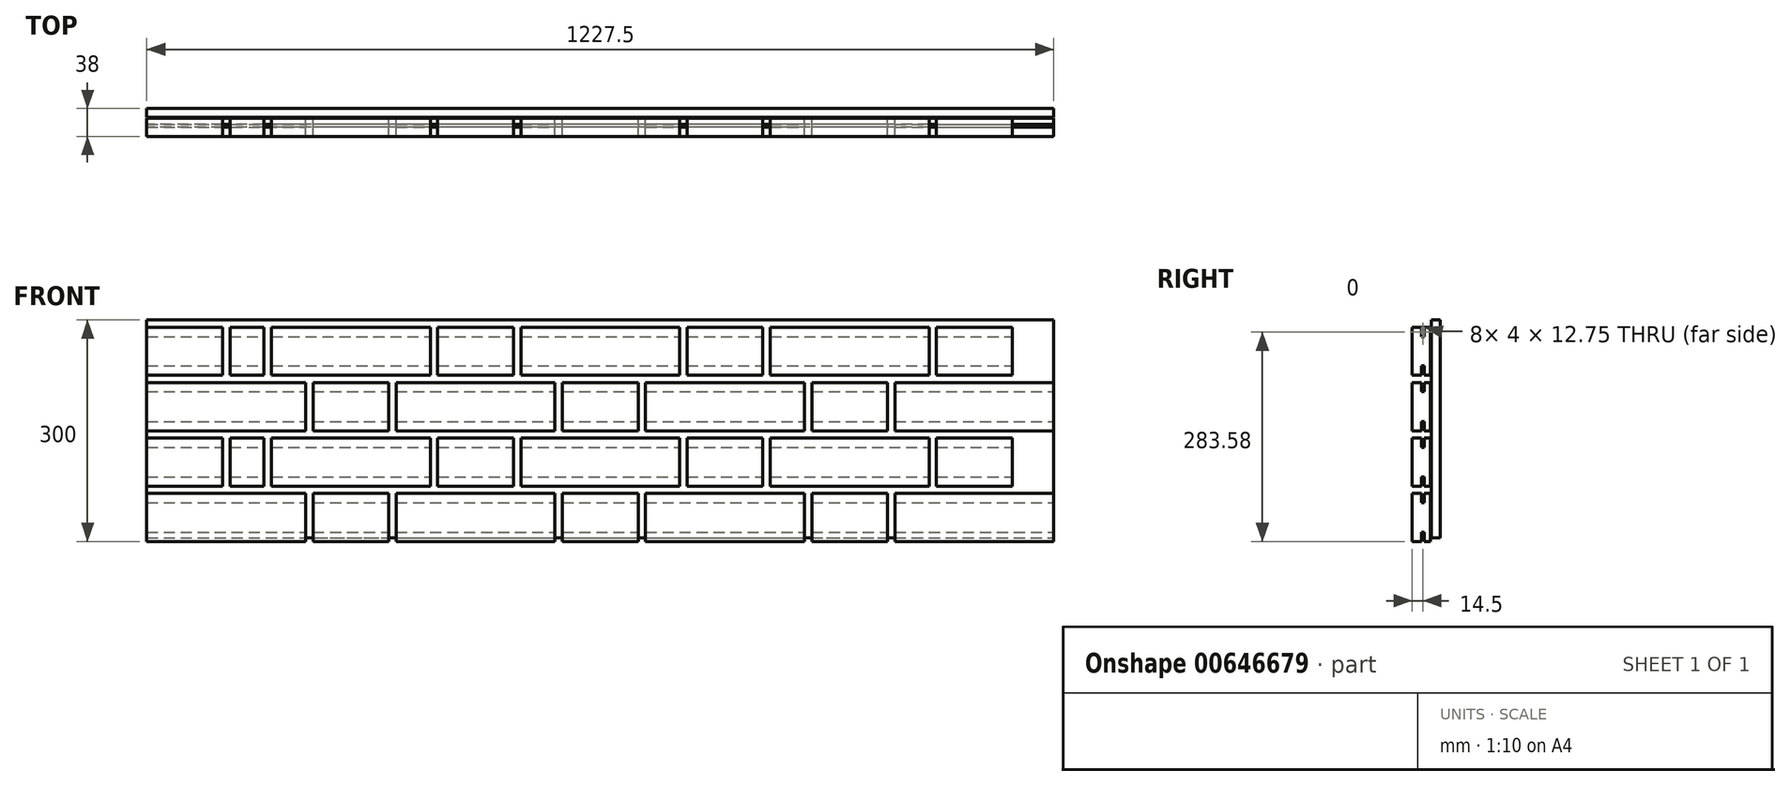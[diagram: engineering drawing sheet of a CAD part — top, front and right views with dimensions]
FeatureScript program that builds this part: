
annotation { "Feature Type Name" : "Feature", "Feature Type Description" : "" }
export const myFeature = defineFeature(function(context is Context, id is Id, definition is map)
    precondition{}
    {
        {
            var Q0;
            Q0=qCreatedBy(makeId("Front.planeOp"),FACE);
            var sketch = newSketch(context, id + "F0", { "sketchPlane" : qUnion([Q0])});
            skLineSegment(sketch, "E0", {"start": v(-1075.67, 0) * mm, "end": v(-1075.67, 65) * mm});
            skLineSegment(sketch, "E1", {"start": v(-1628.17, 150) * mm, "end": v(-1413.17, 150) * mm});
            skLineSegment(sketch, "E2", {"start": v(-1413.17, 150) * mm, "end": v(-1413.17, 215) * mm});
            skLineSegment(sketch, "E3", {"start": v(-1413.17, 215) * mm, "end": v(-1628.17, 215) * mm});
            skLineSegment(sketch, "E4", {"start": v(-1628.17, 215) * mm, "end": v(-1628.17, 150) * mm});
            skLineSegment(sketch, "E5", {"start": v(-1403.17, 150) * mm, "end": v(-1300.67, 150) * mm});
            skLineSegment(sketch, "E6", {"start": v(-1300.67, 150) * mm, "end": v(-1300.67, 215) * mm});
            skLineSegment(sketch, "E7", {"start": v(-1300.67, 215) * mm, "end": v(-1403.17, 215) * mm});
            skLineSegment(sketch, "E8", {"start": v(-1403.17, 215) * mm, "end": v(-1403.17, 150) * mm});
            skLineSegment(sketch, "E9", {"start": v(-1290.67, 150) * mm, "end": v(-1075.67, 150) * mm});
            skLineSegment(sketch, "E10", {"start": v(-1075.67, 150) * mm, "end": v(-1075.67, 215) * mm});
            skLineSegment(sketch, "E11", {"start": v(-1075.67, 215) * mm, "end": v(-1290.67, 215) * mm});
            skLineSegment(sketch, "E12", {"start": v(-1290.67, 215) * mm, "end": v(-1290.67, 150) * mm});
            skLineSegment(sketch, "E13", {"start": v(-2078.17, 150) * mm, "end": v(-1975.67, 150) * mm});
            skLineSegment(sketch, "E14", {"start": v(-1975.67, 150) * mm, "end": v(-1975.67, 215) * mm});
            skLineSegment(sketch, "E15", {"start": v(-1975.67, 215) * mm, "end": v(-2078.17, 215) * mm});
            skLineSegment(sketch, "E16", {"start": v(-2078.17, 215) * mm, "end": v(-2078.17, 150) * mm});
            skLineSegment(sketch, "E17", {"start": v(-1965.67, 150) * mm, "end": v(-1750.67, 150) * mm});
            skLineSegment(sketch, "E18", {"start": v(-1750.67, 150) * mm, "end": v(-1750.67, 215) * mm});
            skLineSegment(sketch, "E19", {"start": v(-1750.67, 215) * mm, "end": v(-1965.67, 215) * mm});
            skLineSegment(sketch, "E20", {"start": v(-1965.67, 215) * mm, "end": v(-1965.67, 150) * mm});
            skLineSegment(sketch, "E21", {"start": v(-1740.67, 150) * mm, "end": v(-1638.17, 150) * mm});
            skLineSegment(sketch, "E22", {"start": v(-1638.17, 150) * mm, "end": v(-1638.17, 215) * mm});
            skLineSegment(sketch, "E23", {"start": v(-1638.17, 215) * mm, "end": v(-1740.67, 215) * mm});
            skLineSegment(sketch, "E24", {"start": v(-1740.67, 215) * mm, "end": v(-1740.67, 150) * mm});
            skLineSegment(sketch, "E25", {"start": v(-2088.17, 150) * mm, "end": v(-2303.17, 150) * mm});
            skLineSegment(sketch, "E26", {"start": v(-2303.17, 150) * mm, "end": v(-2303.17, 215) * mm});
            skLineSegment(sketch, "E27", {"start": v(-2303.17, 215) * mm, "end": v(-2088.17, 215) * mm});
            skLineSegment(sketch, "E28", {"start": v(-2088.17, 215) * mm, "end": v(-2088.17, 150) * mm});
            skLineSegment(sketch, "E29", {"start": v(-2303.17, 225) * mm, "end": v(-2200.67, 225) * mm});
            skLineSegment(sketch, "E30", {"start": v(-2200.67, 225) * mm, "end": v(-2200.67, 290) * mm});
            skLineSegment(sketch, "E31", {"start": v(-2200.67, 290) * mm, "end": v(-2303.17, 290) * mm});
            skLineSegment(sketch, "E32", {"start": v(-2303.17, 290) * mm, "end": v(-2303.17, 225) * mm});
            skLineSegment(sketch, "E33", {"start": v(-2134.42, 225) * mm, "end": v(-1919.42, 225) * mm});
            skLineSegment(sketch, "E34", {"start": v(-1919.42, 225) * mm, "end": v(-1919.42, 290) * mm});
            skLineSegment(sketch, "E35", {"start": v(-1919.42, 290) * mm, "end": v(-2134.42, 290) * mm});
            skLineSegment(sketch, "E36", {"start": v(-2134.42, 290) * mm, "end": v(-2134.42, 225) * mm});
            skLineSegment(sketch, "E37", {"start": v(-1909.42, 225) * mm, "end": v(-1806.92, 225) * mm});
            skLineSegment(sketch, "E38", {"start": v(-1806.92, 225) * mm, "end": v(-1806.92, 290) * mm});
            skLineSegment(sketch, "E39", {"start": v(-1806.92, 290) * mm, "end": v(-1909.42, 290) * mm});
            skLineSegment(sketch, "E40", {"start": v(-1909.42, 290) * mm, "end": v(-1909.42, 225) * mm});
            skLineSegment(sketch, "E41", {"start": v(-2190.67, 225) * mm, "end": v(-2144.37, 225) * mm});
            skLineSegment(sketch, "E42", {"start": v(-2144.37, 225) * mm, "end": v(-2144.37, 290) * mm});
            skLineSegment(sketch, "E43", {"start": v(-2144.37, 290) * mm, "end": v(-2190.67, 290) * mm});
            skLineSegment(sketch, "E44", {"start": v(-2190.67, 290) * mm, "end": v(-2190.67, 225) * mm});
            skLineSegment(sketch, "E45", {"start": v(-1796.92, 225) * mm, "end": v(-1581.92, 225) * mm});
            skLineSegment(sketch, "E46", {"start": v(-1581.92, 225) * mm, "end": v(-1581.92, 290) * mm});
            skLineSegment(sketch, "E47", {"start": v(-1581.92, 290) * mm, "end": v(-1796.92, 290) * mm});
            skLineSegment(sketch, "E48", {"start": v(-1796.92, 290) * mm, "end": v(-1796.92, 225) * mm});
            skLineSegment(sketch, "E49", {"start": v(-1571.92, 225) * mm, "end": v(-1469.42, 225) * mm});
            skLineSegment(sketch, "E50", {"start": v(-1469.42, 225) * mm, "end": v(-1469.42, 290) * mm});
            skLineSegment(sketch, "E51", {"start": v(-1469.42, 290) * mm, "end": v(-1571.92, 290) * mm});
            skLineSegment(sketch, "E52", {"start": v(-1571.92, 290) * mm, "end": v(-1571.92, 225) * mm});
            skLineSegment(sketch, "E53", {"start": v(-1459.42, 225) * mm, "end": v(-1244.42, 225) * mm});
            skLineSegment(sketch, "E54", {"start": v(-1244.42, 225) * mm, "end": v(-1244.42, 290) * mm});
            skLineSegment(sketch, "E55", {"start": v(-1244.42, 290) * mm, "end": v(-1459.42, 290) * mm});
            skLineSegment(sketch, "E56", {"start": v(-1459.42, 290) * mm, "end": v(-1459.42, 225) * mm});
            skLineSegment(sketch, "E57", {"start": v(-1234.42, 225) * mm, "end": v(-1131.92, 225) * mm});
            skLineSegment(sketch, "E58", {"start": v(-1131.92, 225) * mm, "end": v(-1131.92, 290) * mm});
            skLineSegment(sketch, "E59", {"start": v(-1131.92, 290) * mm, "end": v(-1234.42, 290) * mm});
            skLineSegment(sketch, "E60", {"start": v(-1234.42, 290) * mm, "end": v(-1234.42, 225) * mm});
            skLineSegment(sketch, "E61", {"start": v(-1628.17, 65) * mm, "end": v(-1413.17, 65) * mm});
            skLineSegment(sketch, "E62", {"start": v(-1413.17, 65) * mm, "end": v(-1413.17, 0) * mm});
            skLineSegment(sketch, "E63", {"start": v(-1413.17, 0) * mm, "end": v(-1628.17, 0) * mm});
            skLineSegment(sketch, "E64", {"start": v(-1628.17, 0) * mm, "end": v(-1628.17, 65) * mm});
            skLineSegment(sketch, "E65", {"start": v(-1403.17, 65) * mm, "end": v(-1300.67, 65) * mm});
            skLineSegment(sketch, "E66", {"start": v(-1300.67, 65) * mm, "end": v(-1300.67, 0) * mm});
            skLineSegment(sketch, "E67", {"start": v(-1300.67, 0) * mm, "end": v(-1403.17, 0) * mm});
            skLineSegment(sketch, "E68", {"start": v(-1403.17, 0) * mm, "end": v(-1403.17, 65) * mm});
            skLineSegment(sketch, "E69", {"start": v(-1290.67, 65) * mm, "end": v(-1075.67, 65) * mm});
            skLineSegment(sketch, "E70", {"start": v(-1075.67, 65) * mm, "end": v(-1075.67, 0) * mm});
            skLineSegment(sketch, "E71", {"start": v(-1075.67, 0) * mm, "end": v(-1290.67, 0) * mm});
            skLineSegment(sketch, "E72", {"start": v(-1290.67, 0) * mm, "end": v(-1290.67, 65) * mm});
            skLineSegment(sketch, "E73", {"start": v(-2078.17, 65) * mm, "end": v(-1975.67, 65) * mm});
            skLineSegment(sketch, "E74", {"start": v(-1975.67, 65) * mm, "end": v(-1975.67, 0) * mm});
            skLineSegment(sketch, "E75", {"start": v(-1975.67, 0) * mm, "end": v(-2078.17, 0) * mm});
            skLineSegment(sketch, "E76", {"start": v(-2078.17, 0) * mm, "end": v(-2078.17, 65) * mm});
            skLineSegment(sketch, "E77", {"start": v(-1965.67, 65) * mm, "end": v(-1750.67, 65) * mm});
            skLineSegment(sketch, "E78", {"start": v(-1750.67, 65) * mm, "end": v(-1750.67, 0) * mm});
            skLineSegment(sketch, "E79", {"start": v(-1750.67, 0) * mm, "end": v(-1965.67, 0) * mm});
            skLineSegment(sketch, "E80", {"start": v(-1965.67, 0) * mm, "end": v(-1965.67, 65) * mm});
            skLineSegment(sketch, "E81", {"start": v(-1740.67, 65) * mm, "end": v(-1638.17, 65) * mm});
            skLineSegment(sketch, "E82", {"start": v(-1638.17, 65) * mm, "end": v(-1638.17, 0) * mm});
            skLineSegment(sketch, "E83", {"start": v(-1638.17, 0) * mm, "end": v(-1740.67, 0) * mm});
            skLineSegment(sketch, "E84", {"start": v(-1740.67, 0) * mm, "end": v(-1740.67, 65) * mm});
            skLineSegment(sketch, "E85", {"start": v(-2088.17, 65) * mm, "end": v(-2303.17, 65) * mm});
            skLineSegment(sketch, "E86", {"start": v(-2303.17, 65) * mm, "end": v(-2303.17, 0) * mm});
            skLineSegment(sketch, "E87", {"start": v(-2303.17, 0) * mm, "end": v(-2088.17, 0) * mm});
            skLineSegment(sketch, "E88", {"start": v(-2088.17, 0) * mm, "end": v(-2088.17, 65) * mm});
            skLineSegment(sketch, "E89", {"start": v(-2303.17, 140) * mm, "end": v(-2200.67, 140) * mm});
            skLineSegment(sketch, "E90", {"start": v(-2200.67, 140) * mm, "end": v(-2200.67, 75) * mm});
            skLineSegment(sketch, "E91", {"start": v(-2200.67, 75) * mm, "end": v(-2303.17, 75) * mm});
            skLineSegment(sketch, "E92", {"start": v(-2303.17, 75) * mm, "end": v(-2303.17, 140) * mm});
            skLineSegment(sketch, "E93", {"start": v(-2134.42, 140) * mm, "end": v(-1919.42, 140) * mm});
            skLineSegment(sketch, "E94", {"start": v(-1919.42, 140) * mm, "end": v(-1919.42, 75) * mm});
            skLineSegment(sketch, "E95", {"start": v(-1919.42, 75) * mm, "end": v(-2134.42, 75) * mm});
            skLineSegment(sketch, "E96", {"start": v(-2134.42, 75) * mm, "end": v(-2134.42, 140) * mm});
            skLineSegment(sketch, "E97", {"start": v(-1909.42, 140) * mm, "end": v(-1806.92, 140) * mm});
            skLineSegment(sketch, "E98", {"start": v(-1806.92, 140) * mm, "end": v(-1806.92, 75) * mm});
            skLineSegment(sketch, "E99", {"start": v(-1806.92, 75) * mm, "end": v(-1909.42, 75) * mm});
            skLineSegment(sketch, "E100", {"start": v(-1909.42, 75) * mm, "end": v(-1909.42, 140) * mm});
            skLineSegment(sketch, "E101", {"start": v(-2190.67, 140) * mm, "end": v(-2144.37, 140) * mm});
            skLineSegment(sketch, "E102", {"start": v(-2144.37, 140) * mm, "end": v(-2144.37, 75) * mm});
            skLineSegment(sketch, "E103", {"start": v(-2144.37, 75) * mm, "end": v(-2190.67, 75) * mm});
            skLineSegment(sketch, "E104", {"start": v(-2190.67, 75) * mm, "end": v(-2190.67, 140) * mm});
            skLineSegment(sketch, "E105", {"start": v(-1796.92, 140) * mm, "end": v(-1581.92, 140) * mm});
            skLineSegment(sketch, "E106", {"start": v(-1581.92, 140) * mm, "end": v(-1581.92, 75) * mm});
            skLineSegment(sketch, "E107", {"start": v(-1581.92, 75) * mm, "end": v(-1796.92, 75) * mm});
            skLineSegment(sketch, "E108", {"start": v(-1796.92, 75) * mm, "end": v(-1796.92, 140) * mm});
            skLineSegment(sketch, "E109", {"start": v(-1571.92, 140) * mm, "end": v(-1469.42, 140) * mm});
            skLineSegment(sketch, "E110", {"start": v(-1469.42, 140) * mm, "end": v(-1469.42, 75) * mm});
            skLineSegment(sketch, "E111", {"start": v(-1469.42, 75) * mm, "end": v(-1571.92, 75) * mm});
            skLineSegment(sketch, "E112", {"start": v(-1571.92, 75) * mm, "end": v(-1571.92, 140) * mm});
            skLineSegment(sketch, "E113", {"start": v(-1459.42, 140) * mm, "end": v(-1244.42, 140) * mm});
            skLineSegment(sketch, "E114", {"start": v(-1244.42, 140) * mm, "end": v(-1244.42, 75) * mm});
            skLineSegment(sketch, "E115", {"start": v(-1244.42, 75) * mm, "end": v(-1459.42, 75) * mm});
            skLineSegment(sketch, "E116", {"start": v(-1459.42, 75) * mm, "end": v(-1459.42, 140) * mm});
            skLineSegment(sketch, "E117", {"start": v(-1234.42, 140) * mm, "end": v(-1131.92, 140) * mm});
            skLineSegment(sketch, "E118", {"start": v(-1131.92, 140) * mm, "end": v(-1131.92, 75) * mm});
            skLineSegment(sketch, "E119", {"start": v(-1131.92, 75) * mm, "end": v(-1234.42, 75) * mm});
            skLineSegment(sketch, "E120", {"start": v(-1234.42, 75) * mm, "end": v(-1234.42, 140) * mm});
            skSolve(sketch);
        }
        {
            var Q0;
            Q0=makeQuery(id+"F0.imprint","IMPRINT",FACE,{"disambiguationData":[TD([[makeQuery(id+"F0.imprint","IMPRINT",EDGE,{"derivedFrom":sQuery(id+"F0.wireOp",EDGE,"E29")}),1.0]])]});
            var Q1;
            Q1=makeQuery(id+"F0.imprint","IMPRINT",FACE,{"disambiguationData":[TD([[makeQuery(id+"F0.imprint","IMPRINT",EDGE,{"derivedFrom":sQuery(id+"F0.wireOp",EDGE,"E41")}),1.0]])]});
            var Q2;
            Q2=makeQuery(id+"F0.imprint","IMPRINT",FACE,{"disambiguationData":[TD([[makeQuery(id+"F0.imprint","IMPRINT",EDGE,{"derivedFrom":sQuery(id+"F0.wireOp",EDGE,"E33")}),1.0]])]});
            var Q3;
            Q3=makeQuery(id+"F0.imprint","IMPRINT",FACE,{"disambiguationData":[TD([[makeQuery(id+"F0.imprint","IMPRINT",EDGE,{"derivedFrom":sQuery(id+"F0.wireOp",EDGE,"E37")}),1.0]])]});
            var Q4;
            Q4=makeQuery(id+"F0.imprint","IMPRINT",FACE,{"disambiguationData":[TD([[makeQuery(id+"F0.imprint","IMPRINT",EDGE,{"derivedFrom":sQuery(id+"F0.wireOp",EDGE,"E45")}),1.0]])]});
            var Q5;
            Q5=makeQuery(id+"F0.imprint","IMPRINT",FACE,{"disambiguationData":[TD([[makeQuery(id+"F0.imprint","IMPRINT",EDGE,{"derivedFrom":sQuery(id+"F0.wireOp",EDGE,"E49")}),1.0]])]});
            var Q6;
            Q6=makeQuery(id+"F0.imprint","IMPRINT",FACE,{"disambiguationData":[TD([[makeQuery(id+"F0.imprint","IMPRINT",EDGE,{"derivedFrom":sQuery(id+"F0.wireOp",EDGE,"E53")}),1.0]])]});
            var Q7;
            Q7=makeQuery(id+"F0.imprint","IMPRINT",FACE,{"disambiguationData":[TD([[makeQuery(id+"F0.imprint","IMPRINT",EDGE,{"derivedFrom":sQuery(id+"F0.wireOp",EDGE,"E57")}),1.0]])]});
            var Q8;
            Q8=makeQuery(id+"F0.imprint","IMPRINT",FACE,{"disambiguationData":[TD([[makeQuery(id+"F0.imprint","IMPRINT",EDGE,{"derivedFrom":sQuery(id+"F0.wireOp",EDGE,"E9")}),1.0]])]});
            var Q9;
            Q9=makeQuery(id+"F0.imprint","IMPRINT",FACE,{"disambiguationData":[TD([[makeQuery(id+"F0.imprint","IMPRINT",EDGE,{"derivedFrom":sQuery(id+"F0.wireOp",EDGE,"E5")}),1.0]])]});
            var Q10;
            Q10=makeQuery(id+"F0.imprint","IMPRINT",FACE,{"disambiguationData":[TD([[makeQuery(id+"F0.imprint","IMPRINT",EDGE,{"derivedFrom":sQuery(id+"F0.wireOp",EDGE,"E1")}),1.0]])]});
            var Q11;
            Q11=makeQuery(id+"F0.imprint","IMPRINT",FACE,{"disambiguationData":[TD([[makeQuery(id+"F0.imprint","IMPRINT",EDGE,{"derivedFrom":sQuery(id+"F0.wireOp",EDGE,"E21")}),1.0]])]});
            var Q12;
            Q12=makeQuery(id+"F0.imprint","IMPRINT",FACE,{"disambiguationData":[TD([[makeQuery(id+"F0.imprint","IMPRINT",EDGE,{"derivedFrom":sQuery(id+"F0.wireOp",EDGE,"E17")}),1.0]])]});
            var Q13;
            Q13=makeQuery(id+"F0.imprint","IMPRINT",FACE,{"disambiguationData":[TD([[makeQuery(id+"F0.imprint","IMPRINT",EDGE,{"derivedFrom":sQuery(id+"F0.wireOp",EDGE,"E13")}),1.0]])]});
            var Q14;
            Q14=makeQuery(id+"F0.imprint","IMPRINT",FACE,{"disambiguationData":[TD([[makeQuery(id+"F0.imprint","IMPRINT",EDGE,{"derivedFrom":sQuery(id+"F0.wireOp",EDGE,"E25")}),-1.0]])]});
            var Q15;
            Q15=makeQuery(id+"F0.imprint","IMPRINT",FACE,{"disambiguationData":[TD([[makeQuery(id+"F0.imprint","IMPRINT",EDGE,{"derivedFrom":sQuery(id+"F0.wireOp",EDGE,"E89")}),-1.0]])]});
            var Q16;
            Q16=makeQuery(id+"F0.imprint","IMPRINT",FACE,{"disambiguationData":[TD([[makeQuery(id+"F0.imprint","IMPRINT",EDGE,{"derivedFrom":sQuery(id+"F0.wireOp",EDGE,"E101")}),-1.0]])]});
            var Q17;
            Q17=makeQuery(id+"F0.imprint","IMPRINT",FACE,{"disambiguationData":[TD([[makeQuery(id+"F0.imprint","IMPRINT",EDGE,{"derivedFrom":sQuery(id+"F0.wireOp",EDGE,"E93")}),-1.0]])]});
            var Q18;
            Q18=makeQuery(id+"F0.imprint","IMPRINT",FACE,{"disambiguationData":[TD([[makeQuery(id+"F0.imprint","IMPRINT",EDGE,{"derivedFrom":sQuery(id+"F0.wireOp",EDGE,"E97")}),-1.0]])]});
            var Q19;
            Q19=makeQuery(id+"F0.imprint","IMPRINT",FACE,{"disambiguationData":[TD([[makeQuery(id+"F0.imprint","IMPRINT",EDGE,{"derivedFrom":sQuery(id+"F0.wireOp",EDGE,"E105")}),-1.0]])]});
            var Q20;
            Q20=makeQuery(id+"F0.imprint","IMPRINT",FACE,{"disambiguationData":[TD([[makeQuery(id+"F0.imprint","IMPRINT",EDGE,{"derivedFrom":sQuery(id+"F0.wireOp",EDGE,"E109")}),-1.0]])]});
            var Q21;
            Q21=makeQuery(id+"F0.imprint","IMPRINT",FACE,{"disambiguationData":[TD([[makeQuery(id+"F0.imprint","IMPRINT",EDGE,{"derivedFrom":sQuery(id+"F0.wireOp",EDGE,"E113")}),-1.0]])]});
            var Q22;
            Q22=makeQuery(id+"F0.imprint","IMPRINT",FACE,{"disambiguationData":[TD([[makeQuery(id+"F0.imprint","IMPRINT",EDGE,{"derivedFrom":sQuery(id+"F0.wireOp",EDGE,"E117")}),-1.0]])]});
            var Q23;
            Q23=makeQuery(id+"F0.imprint","IMPRINT",FACE,{"disambiguationData":[TD([[makeQuery(id+"F0.imprint","IMPRINT",EDGE,{"derivedFrom":sQuery(id+"F0.wireOp",EDGE,"E69")}),-1.0]])]});
            var Q24;
            Q24=makeQuery(id+"F0.imprint","IMPRINT",FACE,{"disambiguationData":[TD([[makeQuery(id+"F0.imprint","IMPRINT",EDGE,{"derivedFrom":sQuery(id+"F0.wireOp",EDGE,"E65")}),-1.0]])]});
            var Q25;
            Q25=makeQuery(id+"F0.imprint","IMPRINT",FACE,{"disambiguationData":[TD([[makeQuery(id+"F0.imprint","IMPRINT",EDGE,{"derivedFrom":sQuery(id+"F0.wireOp",EDGE,"E61")}),-1.0]])]});
            var Q26;
            Q26=makeQuery(id+"F0.imprint","IMPRINT",FACE,{"disambiguationData":[TD([[makeQuery(id+"F0.imprint","IMPRINT",EDGE,{"derivedFrom":sQuery(id+"F0.wireOp",EDGE,"E81")}),-1.0]])]});
            var Q27;
            Q27=makeQuery(id+"F0.imprint","IMPRINT",FACE,{"disambiguationData":[TD([[makeQuery(id+"F0.imprint","IMPRINT",EDGE,{"derivedFrom":sQuery(id+"F0.wireOp",EDGE,"E77")}),-1.0]])]});
            var Q28;
            Q28=makeQuery(id+"F0.imprint","IMPRINT",FACE,{"disambiguationData":[TD([[makeQuery(id+"F0.imprint","IMPRINT",EDGE,{"derivedFrom":sQuery(id+"F0.wireOp",EDGE,"E73")}),-1.0]])]});
            var Q29;
            Q29=makeQuery(id+"F0.imprint","IMPRINT",FACE,{"disambiguationData":[TD([[makeQuery(id+"F0.imprint","IMPRINT",EDGE,{"derivedFrom":sQuery(id+"F0.wireOp",EDGE,"E85")}),1.0]])]});
            extrude(context, id + "F1", {"entities" : qUnion([Q0, Q1, Q2, Q3, Q4, Q5, Q6, Q7, Q8, Q9, Q10, Q11, Q12, Q13, Q14, Q15, Q16, Q17, Q18, Q19, Q20, Q21, Q22, Q23, Q24, Q25, Q26, Q27, Q28, Q29]), "depth" : 25 * mm, "offsetDistance" : 25 * mm});
        }
        {
            var Q0;
            Q0=makeQuery(id+"F1.opExtrude","SWEPT_FACE",FACE,{"disambiguationData":[OSD([sQuery(id+"F0.wireOp",EDGE,"E10")])]});
            cPlane(context, id + "F2", {"entities" : qUnion([Q0]), "cplaneType" : CPlaneType.OFFSET, "offset" : 0 * mm, "width" : 150 * mm, "height" : 150 * mm});
        }
        {
            var Q0;
            Q0=qCreatedBy(id+"F2.planeOp",FACE);
            var sketch = newSketch(context, id + "F3", { "sketchPlane" : qUnion([Q0])});
            skLineSegment(sketch, "E121.bottom", {"start": v(-12.5, 52.26) * mm, "end": v(-8.5, 52.26) * mm});
            skLineSegment(sketch, "E121.top", {"start": v(-12.5, 87.26) * mm, "end": v(-8.5, 87.26) * mm});
            skLineSegment(sketch, "E121.left", {"start": v(-12.5, 52.26) * mm, "end": v(-12.5, 87.26) * mm});
            skLineSegment(sketch, "E121.right", {"start": v(-8.5, 52.26) * mm, "end": v(-8.5, 87.26) * mm});
            skLineSegment(sketch, "E122.bottom", {"start": v(-12.5, 127.29) * mm, "end": v(-8.5, 127.29) * mm});
            skLineSegment(sketch, "E122.top", {"start": v(-12.5, 162.29) * mm, "end": v(-8.5, 162.29) * mm});
            skLineSegment(sketch, "E122.left", {"start": v(-12.5, 127.29) * mm, "end": v(-12.5, 162.29) * mm});
            skLineSegment(sketch, "E122.right", {"start": v(-8.5, 127.29) * mm, "end": v(-8.5, 162.29) * mm});
            skLineSegment(sketch, "E123.bottom", {"start": v(-12.5, 202.92) * mm, "end": v(-8.5, 202.92) * mm});
            skLineSegment(sketch, "E123.top", {"start": v(-12.5, 237.92) * mm, "end": v(-8.5, 237.92) * mm});
            skLineSegment(sketch, "E123.left", {"start": v(-12.5, 202.92) * mm, "end": v(-12.5, 237.92) * mm});
            skLineSegment(sketch, "E123.right", {"start": v(-8.5, 202.92) * mm, "end": v(-8.5, 237.92) * mm});
            skLineSegment(sketch, "E124.bottom", {"start": v(-12.5, 0) * mm, "end": v(-8.5, 0) * mm});
            skLineSegment(sketch, "E124.top", {"start": v(-12.5, 12.75) * mm, "end": v(-8.5, 12.75) * mm});
            skLineSegment(sketch, "E124.left", {"start": v(-12.5, 0) * mm, "end": v(-12.5, 12.75) * mm});
            skLineSegment(sketch, "E124.right", {"start": v(-8.5, 0) * mm, "end": v(-8.5, 12.75) * mm});
            skLineSegment(sketch, "E125.bottom", {"start": v(-12.5, 277.2) * mm, "end": v(-8.5, 277.2) * mm});
            skLineSegment(sketch, "E125.top", {"start": v(-12.5, 289.95) * mm, "end": v(-8.5, 289.95) * mm});
            skLineSegment(sketch, "E125.left", {"start": v(-12.5, 277.2) * mm, "end": v(-12.5, 289.95) * mm});
            skLineSegment(sketch, "E125.right", {"start": v(-8.5, 277.2) * mm, "end": v(-8.5, 289.95) * mm});
            skSolve(sketch);
        }
        {
            var Q0;
            Q0=qSketchRegion(id+"F3",true);
            extrude(context, id + "F4", {"entities" : qUnion([Q0]), "operationType" : NewBodyOperationType.REMOVE, "endBound" : BoundingType.THROUGH_ALL, "oppositeDirection" : true, "depth" : 25 * mm, "offsetDistance" : 25 * mm});
        }
        {
            var Q0;
            Q0=qCreatedBy(id+"F2.planeOp",FACE);
            var sketch = newSketch(context, id + "F5", { "sketchPlane" : qUnion([Q0])});
            skLineSegment(sketch, "E126.bottom", {"start": v(1, 5) * mm, "end": v(13, 5) * mm});
            skLineSegment(sketch, "E126.top", {"start": v(1, 300) * mm, "end": v(13, 300) * mm});
            skLineSegment(sketch, "E126.left", {"start": v(1, 5) * mm, "end": v(1, 300) * mm});
            skLineSegment(sketch, "E126.right", {"start": v(13, 5) * mm, "end": v(13, 300) * mm});
            skSolve(sketch);
        }
        {
            var Q0;
            Q0=qSketchRegion(id+"F5",true);
            extrude(context, id + "F6", {"entities" : qUnion([Q0]), "oppositeDirection" : true, "depth" : 1227.5 * mm, "offsetDistance" : 25 * mm});
        }
    });
